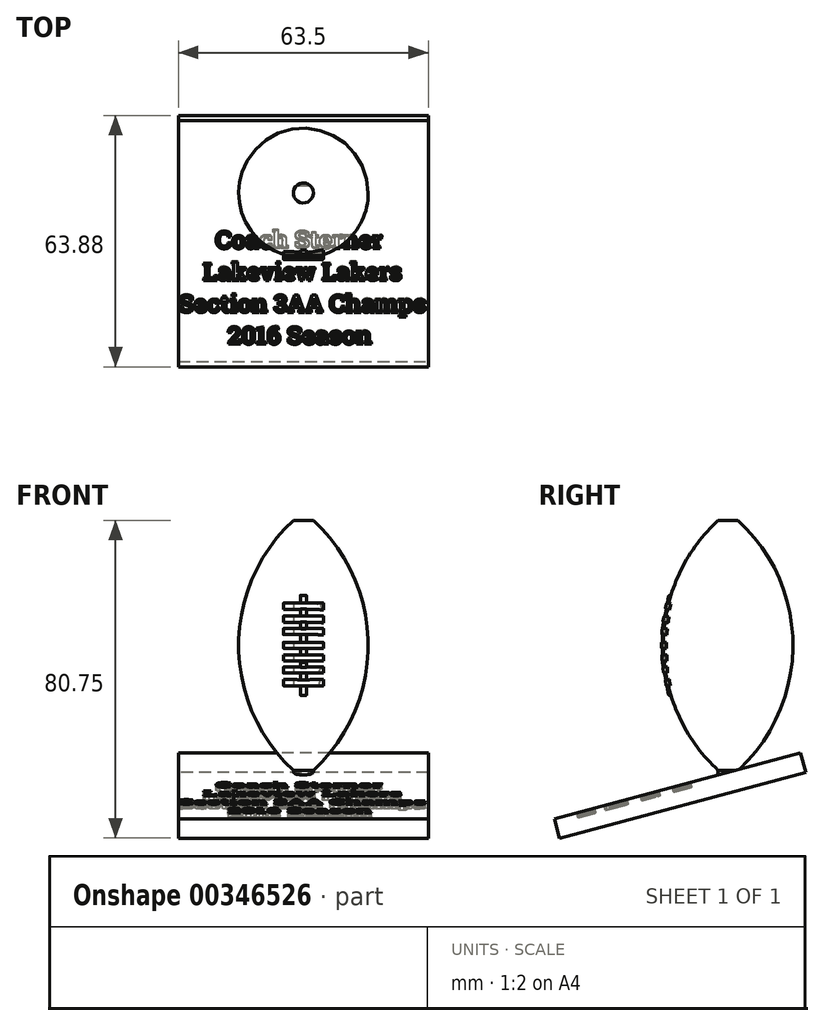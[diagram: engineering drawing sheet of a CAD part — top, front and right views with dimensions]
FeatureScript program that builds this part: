
annotation { "Feature Type Name" : "Feature", "Feature Type Description" : "" }
export const myFeature = defineFeature(function(context is Context, id is Id, definition is map)
    precondition{}
    {
        {
            var Q0;
            Q0=qCreatedBy(makeId("Front.planeOp"),FACE);
            var sketch = newSketch(context, id + "F0", { "sketchPlane" : qUnion([Q0])});
            skLineSegment(sketch, "E0", {"start": v(0, 0) * mm, "end": v(0, 63.5) * mm});
            skLineSegment(sketch, "E1", {"start": v(0, 0) * mm, "end": v(2.54, 0) * mm});
            skLineSegment(sketch, "E2", {"start": v(2.54, 0) * mm, "end": v(2.54, 63.5) * mm});
            skLineSegment(sketch, "E3", {"start": v(2.54, 63.5) * mm, "end": v(0, 63.5) * mm});
            skArc(sketch, "E4", {"start": v(0, 63.5) * mm, "mid": v(-13.91, 31.75) * mm, "end": v(0, 0) * mm});
            skSolve(sketch);
        }
        {
            var Q0;
            Q0=makeQuery(id+"F0.imprint","IMPRINT",FACE,{"disambiguationData":[TD([[makeQuery(id+"F0.imprint","IMPRINT",EDGE,{"derivedFrom":sQuery(id+"F0.wireOp",EDGE,"E0")}),1.0]])]});
            var Q1;
            Q1=sQuery(id+"F0.wireOp",EDGE,"E2");
            revolve(context, id + "F1", {"entities" : qUnion([Q0]), "axis" : qUnion([Q1]), "revolveType" : RevolveType.FULL});
        }
        {
            var Q0;
            Q0=qCreatedBy(makeId("Front.planeOp"),FACE);
            var sketch = newSketch(context, id + "F2", { "sketchPlane" : qUnion([Q0])});
            skLineSegment(sketch, "E5", {"start": v(0, 63.5) * mm, "end": v(2.54, 63.5) * mm});
            skLineSegment(sketch, "E6", {"start": v(0, 63.5) * mm, "end": v(2.03, 65.95) * mm});
            skLineSegment(sketch, "E7", {"start": v(2.03, 65.95) * mm, "end": v(2.54, 65.95) * mm});
            skLineSegment(sketch, "E8", {"start": v(2.54, 65.95) * mm, "end": v(2.54, 63.5) * mm});
            skLineSegment(sketch, "E9.left", {"start": v(0, 63.5) * mm, "end": v(0, 0) * mm});
            skLineSegment(sketch, "E9.right", {"start": v(2.54, 63.5) * mm, "end": v(2.54, 0) * mm});
            skLineSegment(sketch, "E10.bottom", {"start": v(0, 0) * mm, "end": v(2.54, 0) * mm});
            skLineSegment(sketch, "E10.top", {"start": v(0, -2.54) * mm, "end": v(2.54, -2.54) * mm});
            skLineSegment(sketch, "E10.left", {"start": v(0, 0) * mm, "end": v(0, -2.54) * mm});
            skLineSegment(sketch, "E10.right", {"start": v(2.54, 0) * mm, "end": v(2.54, -2.54) * mm});
            skSolve(sketch);
        }
        {
            var Q0;
            Q0=makeQuery(id+"F2.imprint","IMPRINT",FACE,{"disambiguationData":[TD([[makeQuery(id+"F2.imprint","IMPRINT",EDGE,{"derivedFrom":sQuery(id+"F2.wireOp",EDGE,"E5")}),-1.0]])]});
            var Q1;
            Q1=sQuery(id+"F2.wireOp",EDGE,"E9.right");
            revolve(context, id + "F3", {"operationType" : NewBodyOperationType.ADD, "entities" : qUnion([Q0]), "axis" : qUnion([Q1]), "revolveType" : RevolveType.FULL});
        }
        {
            var Q0;
            Q0=makeQuery(id+"F3.opRevolve","SWEPT_FACE",FACE,{"disambiguationData":[OSD([sQuery(id+"F2.wireOp",EDGE,"E10.bottom")])]});
            var sketch = newSketch(context, id + "F4", { "sketchPlane" : qUnion([Q0])});
            skLineSegment(sketch, "E11.bottom", {"start": v(4.34, -1.8) * mm, "end": v(0.74, -1.8) * mm});
            skLineSegment(sketch, "E11.top", {"start": v(4.34, 1.8) * mm, "end": v(0.74, 1.8) * mm});
            skLineSegment(sketch, "E11.left", {"start": v(4.34, -1.8) * mm, "end": v(4.34, 1.8) * mm});
            skLineSegment(sketch, "E11.right", {"start": v(0.74, -1.8) * mm, "end": v(0.74, 1.8) * mm});
            skPoint(sketch, "E11.middle", {"position": v(2.54, 0) * mm});
            skSolve(sketch);
        }
        {
            var Q0;
            Q0=makeQuery(id+"F4.imprint","IMPRINT",FACE,{"disambiguationData":[TD([[makeQuery(id+"F4.imprint","IMPRINT",EDGE,{"derivedFrom":sQuery(id+"F4.wireOp",EDGE,"E11.bottom")}),-1.0]])]});
            extrude(context, id + "F5", {"entities" : qUnion([Q0]), "operationType" : NewBodyOperationType.ADD, "depth" : 2.54 * mm});
        }
        {
            var Q0;
            Q0=makeQuery(id+"F5.opExtrude","CAP_EDGE",EDGE,{"disambiguationData":[OSD([sQuery(id+"F4.wireOp",EDGE,"E11.bottom")])],"isStart":false});
            chamfer(context, id + "F6", {"entities" : qUnion([Q0]), "chamferType" : ChamferType.OFFSET_ANGLE, "width" : 9.4 * mm, "oppositeDirection" : true, "angle" : 15 * degree, "tangentPropagation" : true});
        }
        {
            var Q0;
            Q0=makeQuery(id+"F6.opChamfer","BLEND_FACE",FACE,{"disambiguationData":[OSD([sQuery(id+"F4.wireOp",EDGE,"E11.bottom")])]});
            var sketch = newSketch(context, id + "F7", { "sketchPlane" : qUnion([Q0])});
            skLineSegment(sketch, "E12", {"start": v(2.54, 0.13) * mm, "end": v(2.54, -18.92) * mm});
            skPoint(sketch, "E12.startSnap0", {"position": v(2.54, 1.99) * mm});
            skPoint(sketch, "E12.startSnap1", {"position": v(0.74, 0.13) * mm});
            skLineSegment(sketch, "E13", {"start": v(2.54, -18.92) * mm, "end": v(-29.21, -18.92) * mm});
            skLineSegment(sketch, "E14", {"start": v(-29.21, -18.92) * mm, "end": v(-29.21, 57.28) * mm});
            skLineSegment(sketch, "E15", {"start": v(2.54, -18.92) * mm, "end": v(34.3, -18.92) * mm});
            skLineSegment(sketch, "E16", {"start": v(34.3, -18.92) * mm, "end": v(34.3, 57.28) * mm});
            skLineSegment(sketch, "E17", {"start": v(34.3, 57.28) * mm, "end": v(-29.21, 57.28) * mm});
            skSolve(sketch);
        }
        {
            var Q0;
            Q0=makeQuery(id+"F7.imprint","IMPRINT",FACE,{"disambiguationData":[TD([[makeQuery(id+"F7.imprint","IMPRINT",EDGE,{"derivedFrom":sQuery(id+"F7.wireOp",EDGE,"E13")}),-1.0]])]});
            var Q1;
            {var subQ0=sQuery(id+"F4.wireOp",EDGE,"E11.bottom");var subQ1=makeQuery(id+"F5.opExtrude","CAP_EDGE",EDGE,{"disambiguationData":[OSD([subQ0])],"isStart":false});Q1=makeQuery(id+"F7.imprint","IMPRINT",FACE,{"disambiguationData":[TD([[makeQuery(id+"F7.imprint","IMPRINT",EDGE,{"derivedFrom":makeQuery(id+"F6.opChamfer","BLEND_EDGE",EDGE,{"blendedFrom":[subQ1,makeQuery(id+"F5.opExtrude","SWEPT_FACE",FACE,{"disambiguationData":[OSD([sQuery(id+"F4.wireOp",EDGE,"E11.top")])]})],"blendedInto":[makeQuery(id+"F5.opExtrude","SWEPT_FACE",FACE,{"disambiguationData":[OSD([sQuery(id+"F4.wireOp",EDGE,"E11.top")])]})]})}),-1.0]])]});}
            extrude(context, id + "F8", {"entities" : qUnion([Q0, Q1]), "operationType" : NewBodyOperationType.ADD, "depth" : 5.08 * mm});
        }
        {
            var Q0;
            {var subQ0=makeQuery(id+"F3.opRevolve","SWEPT_FACE",FACE,{"disambiguationData":[OSD([sQuery(id+"F2.wireOp",EDGE,"E10.bottom")])]});Q0=makeQuery(id+"F5.boolean.opBoolean","SPLIT",FACE,{"disambiguationData":[TD([makeQuery(id+"F1.opRevolve","SWEPT_FACE",FACE,{"disambiguationData":[OSD([sQuery(id+"F0.wireOp",EDGE,"E4")])]}),subQ0,makeQuery(id+"F5.opExtrude","SWEPT_FACE",FACE,{"disambiguationData":[OSD([sQuery(id+"F4.wireOp",EDGE,"E11.bottom")])]}),makeQuery(id+"F5.opExtrude","SWEPT_FACE",FACE,{"disambiguationData":[OSD([sQuery(id+"F4.wireOp",EDGE,"E11.top")])]}),makeQuery(id+"F5.opExtrude","SWEPT_FACE",FACE,{"disambiguationData":[OSD([sQuery(id+"F4.wireOp",EDGE,"E11.right")])]})])],"derivedFrom":subQ0});}
            var Q1;
            {var subQ0=makeQuery(id+"F3.opRevolve","SWEPT_FACE",FACE,{"disambiguationData":[OSD([sQuery(id+"F2.wireOp",EDGE,"E10.bottom")])]});Q1=makeQuery(id+"F5.boolean.opBoolean","SPLIT",FACE,{"disambiguationData":[TD([makeQuery(id+"F1.opRevolve","SWEPT_FACE",FACE,{"disambiguationData":[OSD([sQuery(id+"F0.wireOp",EDGE,"E4")])]}),subQ0,makeQuery(id+"F5.opExtrude","SWEPT_FACE",FACE,{"disambiguationData":[OSD([sQuery(id+"F4.wireOp",EDGE,"E11.top")])]}),makeQuery(id+"F5.opExtrude","SWEPT_FACE",FACE,{"disambiguationData":[OSD([sQuery(id+"F4.wireOp",EDGE,"E11.left")])]}),makeQuery(id+"F5.opExtrude","SWEPT_FACE",FACE,{"disambiguationData":[OSD([sQuery(id+"F4.wireOp",EDGE,"E11.right")])]})])],"derivedFrom":subQ0});}
            var Q2;
            {var subQ0=makeQuery(id+"F3.opRevolve","SWEPT_FACE",FACE,{"disambiguationData":[OSD([sQuery(id+"F2.wireOp",EDGE,"E10.bottom")])]});Q2=makeQuery(id+"F5.boolean.opBoolean","SPLIT",FACE,{"disambiguationData":[TD([makeQuery(id+"F1.opRevolve","SWEPT_FACE",FACE,{"disambiguationData":[OSD([sQuery(id+"F0.wireOp",EDGE,"E4")])]}),subQ0,makeQuery(id+"F5.opExtrude","SWEPT_FACE",FACE,{"disambiguationData":[OSD([sQuery(id+"F4.wireOp",EDGE,"E11.bottom")])]}),makeQuery(id+"F5.opExtrude","SWEPT_FACE",FACE,{"disambiguationData":[OSD([sQuery(id+"F4.wireOp",EDGE,"E11.top")])]}),makeQuery(id+"F5.opExtrude","SWEPT_FACE",FACE,{"disambiguationData":[OSD([sQuery(id+"F4.wireOp",EDGE,"E11.left")])]})])],"derivedFrom":subQ0});}
            extrude(context, id + "F9", {"entities" : qUnion([Q0, Q1, Q2]), "operationType" : NewBodyOperationType.ADD, "depth" : 2.54 * mm});
        }
        {
            var Q0;
            Q0=makeQuery(id+"F8.opExtrude","CAP_FACE",FACE,{"disambiguationData":[OSD([sQuery(id+"F7.wireOp",EDGE,"E13"),sQuery(id+"F7.wireOp",EDGE,"E14"),sQuery(id+"F7.wireOp",EDGE,"E15"),sQuery(id+"F7.wireOp",EDGE,"E16"),sQuery(id+"F7.wireOp",EDGE,"E17")])],"isStart":true});
            var sketch = newSketch(context, id + "F10", { "sketchPlane" : qUnion([Q0])});
            skText(sketch, "E18", { "text": "      Coach Sterner\n    Lakeview Lakers\nSection 3AA Champs \n        2016 Season\n", "fontName": "RobotoSlab-Bold.ttf"});
            const initialGuessF10  = {"E18": [-0.02917, -0.01476, 1, 0, 0.00457]};
            skSetInitialGuess(sketch, initialGuessF10);
            skSolve(sketch);
        }
        {
            var Q0;
            Q0 = qSketchRegion(id + "F10", true);
            extrude(context, id + "F11", {"entities" : qUnion([Q0]), "operationType" : NewBodyOperationType.REMOVE, "oppositeDirection" : true, "depth" : 1.27 * mm});
        }
        {
            var Q0;
            {var subQ0=sQuery(id+"F0.wireOp",EDGE,"E4");var subQ1=makeQuery(id+"F1.opRevolve","SWEPT_FACE",FACE,{"disambiguationData":[OSD([subQ0])]});var subQ13=sQuery(id+"F7.wireOp",EDGE,"E17");var subQ14=sQuery(id+"F7.wireOp",EDGE,"E14");var subQ15=sQuery(id+"F7.wireOp",EDGE,"E16");var subQ16=sQuery(id+"F7.wireOp",EDGE,"E15");var subQ17=sQuery(id+"F7.wireOp",EDGE,"E13");Q0=makeQuery(id+"F11.boolean.opBoolean","SPLIT",FACE,{"disambiguationData":[TD([subQ1])],"derivedFrom":makeQuery(id+"F8.opExtrude","CAP_FACE",FACE,{"disambiguationData":[OSD([subQ17,subQ14,subQ16,subQ15,subQ13])],"isStart":true})});}
            var sketch = newSketch(context, id + "F12", { "sketchPlane" : qUnion([Q0])});
            skLineSegment(sketch, "E19.bottom", {"start": v(34.3, -57.28) * mm, "end": v(-29.21, -57.28) * mm});
            skLineSegment(sketch, "E19.top", {"start": v(34.29, -45.85) * mm, "end": v(-29.21, -45.85) * mm});
            skLineSegment(sketch, "E19.left", {"start": v(34.3, -57.28) * mm, "end": v(34.3, -45.85) * mm});
            skLineSegment(sketch, "E19.right", {"start": v(-29.21, -57.28) * mm, "end": v(-29.21, -45.85) * mm});
            skSolve(sketch);
        }
        {
            var Q0;
            Q0=makeQuery(id+"F12.imprint","IMPRINT",FACE,{"disambiguationData":[TD([[makeQuery(id+"F12.imprint","IMPRINT",EDGE,{"derivedFrom":sQuery(id+"F12.wireOp",EDGE,"E19.bottom")}),-1.0]])]});
            extrude(context, id + "F13", {"entities" : qUnion([Q0]), "operationType" : NewBodyOperationType.REMOVE, "oppositeDirection" : true, "depth" : 25.4 * mm});
        }
        {
            var Q0;
            Q0=qCreatedBy(makeId("Right.planeOp"),FACE);
            var sketch = newSketch(context, id + "F14", { "sketchPlane" : qUnion([Q0])});
            skLineSegment(sketch, "E20", {"start": v(0, 0) * mm, "end": v(0, 63.5) * mm});
            skLineSegment(sketch, "E21", {"start": v(0, 63.5) * mm, "end": v(-3.05, 63.5) * mm});
            skLineSegment(sketch, "E22", {"start": v(-3.05, 63.5) * mm, "end": v(-3.05, 0) * mm});
            skLineSegment(sketch, "E23", {"start": v(-3.05, 0) * mm, "end": v(0, 0) * mm});
            skArc(sketch, "E24", {"start": v(-3.05, 63.5) * mm, "mid": v(-16.96, 31.75) * mm, "end": v(-3.05, 0) * mm});
            skLineSegment(sketch, "E25.bottom", {"start": v(-16.96, 32.51) * mm, "end": v(-15.63, 32.51) * mm});
            skLineSegment(sketch, "E25.top", {"start": v(-16.96, 30.99) * mm, "end": v(-15.63, 30.99) * mm});
            skLineSegment(sketch, "E25.left", {"start": v(-16.96, 32.51) * mm, "end": v(-16.96, 30.99) * mm});
            skLineSegment(sketch, "E25.right", {"start": v(-15.63, 32.51) * mm, "end": v(-15.63, 30.99) * mm});
            skLineSegment(sketch, "E26", {"start": v(-15.2, 34.39) * mm, "end": v(-15.08, 35.9) * mm});
            skLineSegment(sketch, "E27", {"start": v(-15.08, 35.9) * mm, "end": v(-16.75, 36.04) * mm});
            skLineSegment(sketch, "E28", {"start": v(-16.75, 36.04) * mm, "end": v(-16.87, 34.52) * mm});
            skLineSegment(sketch, "E29", {"start": v(-16.87, 34.52) * mm, "end": v(-15.2, 34.39) * mm});
            skLineSegment(sketch, "E30", {"start": v(-16.55, 37.68) * mm, "end": v(-16.32, 39.19) * mm});
            skLineSegment(sketch, "E31", {"start": v(-16.32, 39.19) * mm, "end": v(-14.98, 38.98) * mm});
            skLineSegment(sketch, "E32", {"start": v(-14.98, 38.98) * mm, "end": v(-15.21, 37.47) * mm});
            skLineSegment(sketch, "E33", {"start": v(-15.21, 37.47) * mm, "end": v(-16.55, 37.68) * mm});
            skLineSegment(sketch, "E34", {"start": v(-16.9, 29.29) * mm, "end": v(-15.57, 29.29) * mm});
            skLineSegment(sketch, "E35", {"start": v(-15.57, 29.29) * mm, "end": v(-15.57, 27.77) * mm});
            skLineSegment(sketch, "E36", {"start": v(-15.57, 27.77) * mm, "end": v(-16.78, 27.77) * mm});
            skLineSegment(sketch, "E37", {"start": v(-16.78, 27.77) * mm, "end": v(-16.9, 29.29) * mm});
            skLineSegment(sketch, "E38", {"start": v(-16.6, 26.22) * mm, "end": v(-15.46, 26.22) * mm});
            skLineSegment(sketch, "E39", {"start": v(-15.46, 26.22) * mm, "end": v(-15.46, 24.7) * mm});
            skLineSegment(sketch, "E40", {"start": v(-15.46, 24.7) * mm, "end": v(-16.38, 24.7) * mm});
            skLineSegment(sketch, "E41", {"start": v(-16.38, 24.7) * mm, "end": v(-16.6, 26.22) * mm});
            skLineSegment(sketch, "E42", {"start": v(-15.95, 41.04) * mm, "end": v(-15.6, 42.52) * mm});
            skLineSegment(sketch, "E43", {"start": v(-15.6, 42.52) * mm, "end": v(-14.5, 42.26) * mm});
            skLineSegment(sketch, "E44", {"start": v(-14.5, 42.26) * mm, "end": v(-14.86, 40.78) * mm});
            skLineSegment(sketch, "E45", {"start": v(-14.86, 40.78) * mm, "end": v(-15.95, 41.04) * mm});
            skLineSegment(sketch, "E46", {"start": v(-16.05, 22.93) * mm, "end": v(-15.7, 21.42) * mm});
            skLineSegment(sketch, "E47", {"start": v(-15.7, 21.42) * mm, "end": v(-14.71, 21.6) * mm});
            skLineSegment(sketch, "E48", {"start": v(-14.71, 21.6) * mm, "end": v(-14.98, 23.1) * mm});
            skLineSegment(sketch, "E49", {"start": v(-14.98, 23.1) * mm, "end": v(-16.05, 22.93) * mm});
            skSolve(sketch);
        }
        {
            var Q0;
            Q0=makeQuery(id+"F14.imprint","IMPRINT",FACE,{"disambiguationData":[TD([[makeQuery(id+"F14.imprint","IMPRINT",EDGE,{"derivedFrom":sQuery(id+"F14.wireOp",EDGE,"E42")}),-1.0]])]});
            var Q1;
            {var subQ0=sQuery(id+"F14.wireOp",EDGE,"E32");Q1=makeQuery(id+"F14.imprint","IMPRINT",FACE,{"disambiguationData":[TD([[makeQuery(id+"F14.imprint","IMPRINT",EDGE,{"derivedFrom":subQ0}),-1.0]])]});}
            var Q2;
            Q2=makeQuery(id+"F14.imprint","IMPRINT",FACE,{"disambiguationData":[TD([[makeQuery(id+"F14.imprint","IMPRINT",EDGE,{"derivedFrom":sQuery(id+"F14.wireOp",EDGE,"E26")}),1.0]])]});
            var Q3;
            Q3=makeQuery(id+"F14.imprint","IMPRINT",FACE,{"disambiguationData":[TD([[makeQuery(id+"F14.imprint","IMPRINT",EDGE,{"derivedFrom":sQuery(id+"F14.wireOp",EDGE,"E25.bottom")}),-1.0]])]});
            var Q4;
            Q4=makeQuery(id+"F14.imprint","IMPRINT",FACE,{"disambiguationData":[TD([[makeQuery(id+"F14.imprint","IMPRINT",EDGE,{"derivedFrom":sQuery(id+"F14.wireOp",EDGE,"E34")}),-1.0]])]});
            var Q5;
            Q5=makeQuery(id+"F14.imprint","IMPRINT",FACE,{"disambiguationData":[TD([[makeQuery(id+"F14.imprint","IMPRINT",EDGE,{"derivedFrom":sQuery(id+"F14.wireOp",EDGE,"E38")}),-1.0]])]});
            var Q6;
            Q6=makeQuery(id+"F14.imprint","IMPRINT",FACE,{"disambiguationData":[TD([[makeQuery(id+"F14.imprint","IMPRINT",EDGE,{"derivedFrom":sQuery(id+"F14.wireOp",EDGE,"E46")}),1.0]])]});
            extrude(context, id + "F15", {"entities" : qUnion([Q0, Q1, Q2, Q3, Q4, Q5, Q6]), "operationType" : NewBodyOperationType.ADD, "depth" : 7.62 * mm});
        }
        {
            var Q0;
            Q0=makeQuery(id+"F15.opExtrude","CAP_FACE",FACE,{"disambiguationData":[OSD([sQuery(id+"F14.wireOp",EDGE,"E42"),sQuery(id+"F14.wireOp",EDGE,"E43"),sQuery(id+"F14.wireOp",EDGE,"E44"),sQuery(id+"F14.wireOp",EDGE,"E45")])],"isStart":true});
            var Q1;
            Q1=makeQuery(id+"F15.opExtrude","CAP_FACE",FACE,{"disambiguationData":[OSD([sQuery(id+"F14.wireOp",EDGE,"E24"),sQuery(id+"F14.wireOp",EDGE,"E30"),sQuery(id+"F14.wireOp",EDGE,"E31"),sQuery(id+"F14.wireOp",EDGE,"E32"),sQuery(id+"F14.wireOp",EDGE,"E33")])],"isStart":true});
            var Q2;
            Q2=makeQuery(id+"F15.opExtrude","CAP_FACE",FACE,{"disambiguationData":[OSD([sQuery(id+"F14.wireOp",EDGE,"E26"),sQuery(id+"F14.wireOp",EDGE,"E27"),sQuery(id+"F14.wireOp",EDGE,"E28"),sQuery(id+"F14.wireOp",EDGE,"E29")])],"isStart":true});
            var Q3;
            Q3=makeQuery(id+"F15.opExtrude","CAP_FACE",FACE,{"disambiguationData":[OSD([sQuery(id+"F14.wireOp",EDGE,"E25.bottom"),sQuery(id+"F14.wireOp",EDGE,"E25.top"),sQuery(id+"F14.wireOp",EDGE,"E25.left"),sQuery(id+"F14.wireOp",EDGE,"E25.right")])],"isStart":true});
            var Q4;
            Q4=makeQuery(id+"F15.opExtrude","CAP_FACE",FACE,{"disambiguationData":[OSD([sQuery(id+"F14.wireOp",EDGE,"E34"),sQuery(id+"F14.wireOp",EDGE,"E35"),sQuery(id+"F14.wireOp",EDGE,"E36"),sQuery(id+"F14.wireOp",EDGE,"E37")])],"isStart":true});
            var Q5;
            Q5=makeQuery(id+"F15.opExtrude","CAP_FACE",FACE,{"disambiguationData":[OSD([sQuery(id+"F14.wireOp",EDGE,"E38"),sQuery(id+"F14.wireOp",EDGE,"E39"),sQuery(id+"F14.wireOp",EDGE,"E40"),sQuery(id+"F14.wireOp",EDGE,"E41")])],"isStart":true});
            var Q6;
            Q6=makeQuery(id+"F15.opExtrude","CAP_FACE",FACE,{"disambiguationData":[OSD([sQuery(id+"F14.wireOp",EDGE,"E46"),sQuery(id+"F14.wireOp",EDGE,"E47"),sQuery(id+"F14.wireOp",EDGE,"E48"),sQuery(id+"F14.wireOp",EDGE,"E49")])],"isStart":true});
            extrude(context, id + "F16", {"entities" : qUnion([Q0, Q1, Q2, Q3, Q4, Q5, Q6]), "operationType" : NewBodyOperationType.ADD, "depth" : 2.54 * mm});
        }
        {
            var Q0;
            {var subQ0=sQuery(id+"F14.wireOp",EDGE,"E25.left");Q0=makeQuery(id+"F16.boolean.opBoolean","MERGE",FACE,{"derivedFrom":[makeQuery(id+"F15.opExtrude","SWEPT_FACE",FACE,{"disambiguationData":[OSD([subQ0])]}),makeQuery(id+"F16.opExtrude","SWEPT_FACE",FACE,{"disambiguationData":[OSD([subQ0])]})]});}
            var sketch = newSketch(context, id + "F17", { "sketchPlane" : qUnion([Q0])});
            skLineSegment(sketch, "E50.bottom", {"start": v(3.3, 19.05) * mm, "end": v(1.78, 19.05) * mm});
            skLineSegment(sketch, "E50.top", {"start": v(3.3, 44.45) * mm, "end": v(1.78, 44.45) * mm});
            skLineSegment(sketch, "E50.left", {"start": v(3.3, 19.05) * mm, "end": v(3.3, 44.45) * mm});
            skLineSegment(sketch, "E50.right", {"start": v(1.78, 19.05) * mm, "end": v(1.78, 44.45) * mm});
            skPoint(sketch, "E50.middle", {"position": v(2.54, 31.75) * mm});
            skPoint(sketch, "E50.middle.positionSnap0", {"position": v(7.62, 31.75) * mm});
            skPoint(sketch, "E50.middle.positionSnap1", {"position": v(2.54, 32.51) * mm});
            skPoint(sketch, "E50.centerSnap0", {"position": v(7.62, 31.75) * mm});
            skPoint(sketch, "E50.centerSnap1", {"position": v(2.54, 32.51) * mm});
            skSolve(sketch);
        }
        {
            var Q0;
            {var subQ0=sQuery(id+"F17.wireOp",EDGE,"E50.top");Q0=makeQuery(id+"F17.imprint","IMPRINT",FACE,{"disambiguationData":[TD([[makeQuery(id+"F17.imprint","IMPRINT",EDGE,{"derivedFrom":subQ0}),1.0]])]});}
            var Q1;
            {var subQ0=sQuery(id+"F17.wireOp",EDGE,"E50.bottom");Q1=makeQuery(id+"F17.imprint","IMPRINT",FACE,{"disambiguationData":[TD([[makeQuery(id+"F17.imprint","IMPRINT",EDGE,{"derivedFrom":subQ0}),-1.0]])]});}
            var Q2;
            {var subQ0=sQuery(id+"F17.wireOp",EDGE,"E50.left");var subQ1=sQuery(id+"F14.wireOp",EDGE,"E25.left");var subQ2=sQuery(id+"F14.wireOp",EDGE,"E25.top");var subQ3=sQuery(id+"F14.wireOp",EDGE,"E24");var subQ4=makeQuery(id+"F16.boolean.opBoolean","MERGE",EDGE,{"derivedFrom":[makeQuery(id+"F15.opExtrude","SWEPT_EDGE",EDGE,{"disambiguationData":[OSD([subQ3,subQ2,subQ1])]}),makeQuery(id+"F16.opExtrude","SWEPT_EDGE",EDGE,{"disambiguationData":[OSD([subQ3,subQ2,subQ1])]})]});var subQ5=makeQuery(id+"F17.imprint","INTERSECT",VERTEX,{"derivedFrom":[subQ4,subQ0]});Q2=makeQuery(id+"F17.imprint","IMPRINT",FACE,{"disambiguationData":[TD([[makeQuery(id+"F17.imprint","IMPRINT",EDGE,{"disambiguationData":[TD([[subQ5,-1.0]])],"derivedFrom":subQ0}),1.0]])]});}
            extrude(context, id + "F18", {"entities" : qUnion([Q0, Q1, Q2]), "operationType" : NewBodyOperationType.ADD, "oppositeDirection" : true, "depth" : 2.54 * mm});
        }
        {
            var Q0;
            {var subQ0=sQuery(id+"F14.wireOp",EDGE,"E31");var subQ1=sQuery(id+"F14.wireOp",EDGE,"E24");Q0=makeQuery(id+"F18.boolean.opBoolean","SPLIT",EDGE,{"disambiguationData":[TD([makeQuery(id+"F18.opExtrude","SWEPT_FACE",FACE,{"disambiguationData":[OSD([sQuery(id+"F17.wireOp",EDGE,"E50.left")])]})])],"derivedFrom":makeQuery(id+"F16.boolean.opBoolean","MERGE",EDGE,{"derivedFrom":[makeQuery(id+"F15.opExtrude","SWEPT_EDGE",EDGE,{"disambiguationData":[OSD([subQ1,subQ0])]}),makeQuery(id+"F16.opExtrude","SWEPT_EDGE",EDGE,{"disambiguationData":[OSD([subQ1,subQ0])]})]})});}
            var Q1;
            Q1=makeQuery(id+"F15.opExtrude","CAP_EDGE",EDGE,{"disambiguationData":[OSD([sQuery(id+"F14.wireOp",EDGE,"E30")])],"isStart":false});
            var Q2;
            {var subQ0=sQuery(id+"F14.wireOp",EDGE,"E33");var subQ1=sQuery(id+"F14.wireOp",EDGE,"E30");var subQ2=sQuery(id+"F14.wireOp",EDGE,"E24");Q2=makeQuery(id+"F18.boolean.opBoolean","SPLIT",EDGE,{"disambiguationData":[TD([makeQuery(id+"F18.opExtrude","SWEPT_FACE",FACE,{"disambiguationData":[OSD([sQuery(id+"F17.wireOp",EDGE,"E50.left")])]})])],"derivedFrom":makeQuery(id+"F16.boolean.opBoolean","MERGE",EDGE,{"derivedFrom":[makeQuery(id+"F15.opExtrude","SWEPT_EDGE",EDGE,{"disambiguationData":[OSD([subQ2,subQ1,subQ0])]}),makeQuery(id+"F16.opExtrude","SWEPT_EDGE",EDGE,{"disambiguationData":[OSD([subQ2,subQ1,subQ0])]})]})});}
            var Q3;
            {var subQ0=sQuery(id+"F14.wireOp",EDGE,"E31");var subQ1=sQuery(id+"F14.wireOp",EDGE,"E24");Q3=makeQuery(id+"F18.boolean.opBoolean","SPLIT",EDGE,{"disambiguationData":[TD([makeQuery(id+"F18.opExtrude","SWEPT_FACE",FACE,{"disambiguationData":[OSD([sQuery(id+"F17.wireOp",EDGE,"E50.right")])]})])],"derivedFrom":makeQuery(id+"F16.boolean.opBoolean","MERGE",EDGE,{"derivedFrom":[makeQuery(id+"F15.opExtrude","SWEPT_EDGE",EDGE,{"disambiguationData":[OSD([subQ1,subQ0])]}),makeQuery(id+"F16.opExtrude","SWEPT_EDGE",EDGE,{"disambiguationData":[OSD([subQ1,subQ0])]})]})});}
            var Q4;
            {var subQ0=sQuery(id+"F14.wireOp",EDGE,"E33");var subQ1=sQuery(id+"F14.wireOp",EDGE,"E30");var subQ2=sQuery(id+"F14.wireOp",EDGE,"E24");Q4=makeQuery(id+"F18.boolean.opBoolean","SPLIT",EDGE,{"disambiguationData":[TD([makeQuery(id+"F18.opExtrude","SWEPT_FACE",FACE,{"disambiguationData":[OSD([sQuery(id+"F17.wireOp",EDGE,"E50.right")])]})])],"derivedFrom":makeQuery(id+"F16.boolean.opBoolean","MERGE",EDGE,{"derivedFrom":[makeQuery(id+"F15.opExtrude","SWEPT_EDGE",EDGE,{"disambiguationData":[OSD([subQ2,subQ1,subQ0])]}),makeQuery(id+"F16.opExtrude","SWEPT_EDGE",EDGE,{"disambiguationData":[OSD([subQ2,subQ1,subQ0])]})]})});}
            var Q5;
            Q5=makeQuery(id+"F16.opExtrude","CAP_EDGE",EDGE,{"disambiguationData":[OSD([sQuery(id+"F14.wireOp",EDGE,"E30")])],"isStart":false});
            var Q6;
            Q6=makeQuery(id+"F16.opExtrude","CAP_EDGE",EDGE,{"disambiguationData":[OSD([sQuery(id+"F14.wireOp",EDGE,"E24")])],"isStart":false});
            var Q7;
            Q7=makeQuery(id+"F15.opExtrude","CAP_EDGE",EDGE,{"disambiguationData":[OSD([sQuery(id+"F14.wireOp",EDGE,"E24")])],"isStart":false});
            var Q8;
            {var subQ0=sQuery(id+"F14.wireOp",EDGE,"E43");var subQ1=sQuery(id+"F14.wireOp",EDGE,"E42");var subQ2=sQuery(id+"F14.wireOp",EDGE,"E24");Q8=makeQuery(id+"F18.boolean.opBoolean","SPLIT",EDGE,{"disambiguationData":[TD([makeQuery(id+"F18.opExtrude","SWEPT_FACE",FACE,{"disambiguationData":[OSD([sQuery(id+"F17.wireOp",EDGE,"E50.right")])]})])],"derivedFrom":makeQuery(id+"F16.boolean.opBoolean","MERGE",EDGE,{"derivedFrom":[makeQuery(id+"F15.opExtrude","SWEPT_EDGE",EDGE,{"disambiguationData":[OSD([subQ2,subQ1,subQ0])]}),makeQuery(id+"F16.opExtrude","SWEPT_EDGE",EDGE,{"disambiguationData":[OSD([subQ2,subQ1,subQ0])]})]})});}
            var Q9;
            {var subQ0=sQuery(id+"F14.wireOp",EDGE,"E42");var subQ1=sQuery(id+"F14.wireOp",EDGE,"E45");var subQ2=sQuery(id+"F14.wireOp",EDGE,"E24");Q9=makeQuery(id+"F18.boolean.opBoolean","SPLIT",EDGE,{"disambiguationData":[TD([makeQuery(id+"F18.opExtrude","SWEPT_FACE",FACE,{"disambiguationData":[OSD([sQuery(id+"F17.wireOp",EDGE,"E50.right")])]})])],"derivedFrom":makeQuery(id+"F16.boolean.opBoolean","MERGE",EDGE,{"derivedFrom":[makeQuery(id+"F15.opExtrude","SWEPT_EDGE",EDGE,{"disambiguationData":[OSD([subQ2,subQ0,subQ1])]}),makeQuery(id+"F16.opExtrude","SWEPT_EDGE",EDGE,{"disambiguationData":[OSD([subQ2,subQ0,subQ1])]})]})});}
            var Q10;
            Q10=makeQuery(id+"F16.opExtrude","CAP_EDGE",EDGE,{"disambiguationData":[OSD([sQuery(id+"F14.wireOp",EDGE,"E42")])],"isStart":false});
            var Q11;
            {var subQ0=sQuery(id+"F14.wireOp",EDGE,"E43");var subQ1=sQuery(id+"F14.wireOp",EDGE,"E42");var subQ2=sQuery(id+"F14.wireOp",EDGE,"E24");Q11=makeQuery(id+"F18.boolean.opBoolean","SPLIT",EDGE,{"disambiguationData":[TD([makeQuery(id+"F18.opExtrude","SWEPT_FACE",FACE,{"disambiguationData":[OSD([sQuery(id+"F17.wireOp",EDGE,"E50.left")])]})])],"derivedFrom":makeQuery(id+"F16.boolean.opBoolean","MERGE",EDGE,{"derivedFrom":[makeQuery(id+"F15.opExtrude","SWEPT_EDGE",EDGE,{"disambiguationData":[OSD([subQ2,subQ1,subQ0])]}),makeQuery(id+"F16.opExtrude","SWEPT_EDGE",EDGE,{"disambiguationData":[OSD([subQ2,subQ1,subQ0])]})]})});}
            var Q12;
            {var subQ0=sQuery(id+"F14.wireOp",EDGE,"E42");var subQ1=sQuery(id+"F14.wireOp",EDGE,"E45");var subQ2=sQuery(id+"F14.wireOp",EDGE,"E24");Q12=makeQuery(id+"F18.boolean.opBoolean","SPLIT",EDGE,{"disambiguationData":[TD([makeQuery(id+"F18.opExtrude","SWEPT_FACE",FACE,{"disambiguationData":[OSD([sQuery(id+"F17.wireOp",EDGE,"E50.left")])]})])],"derivedFrom":makeQuery(id+"F16.boolean.opBoolean","MERGE",EDGE,{"derivedFrom":[makeQuery(id+"F15.opExtrude","SWEPT_EDGE",EDGE,{"disambiguationData":[OSD([subQ2,subQ0,subQ1])]}),makeQuery(id+"F16.opExtrude","SWEPT_EDGE",EDGE,{"disambiguationData":[OSD([subQ2,subQ0,subQ1])]})]})});}
            var Q13;
            Q13=makeQuery(id+"F15.opExtrude","CAP_EDGE",EDGE,{"disambiguationData":[OSD([sQuery(id+"F14.wireOp",EDGE,"E42")])],"isStart":false});
            var Q14;
            {var subQ0=sQuery(id+"F14.wireOp",EDGE,"E28");var subQ1=sQuery(id+"F14.wireOp",EDGE,"E27");var subQ2=sQuery(id+"F14.wireOp",EDGE,"E24");Q14=makeQuery(id+"F18.boolean.opBoolean","SPLIT",EDGE,{"disambiguationData":[TD([makeQuery(id+"F18.opExtrude","SWEPT_FACE",FACE,{"disambiguationData":[OSD([sQuery(id+"F17.wireOp",EDGE,"E50.right")])]})])],"derivedFrom":makeQuery(id+"F16.boolean.opBoolean","MERGE",EDGE,{"derivedFrom":[makeQuery(id+"F15.opExtrude","SWEPT_EDGE",EDGE,{"disambiguationData":[OSD([subQ2,subQ1,subQ0])]}),makeQuery(id+"F16.opExtrude","SWEPT_EDGE",EDGE,{"disambiguationData":[OSD([subQ2,subQ1,subQ0])]})]})});}
            var Q15;
            Q15=makeQuery(id+"F16.opExtrude","CAP_EDGE",EDGE,{"disambiguationData":[OSD([sQuery(id+"F14.wireOp",EDGE,"E28")])],"isStart":false});
            var Q16;
            {var subQ0=sQuery(id+"F14.wireOp",EDGE,"E28");var subQ1=sQuery(id+"F14.wireOp",EDGE,"E29");var subQ2=sQuery(id+"F14.wireOp",EDGE,"E24");Q16=makeQuery(id+"F18.boolean.opBoolean","SPLIT",EDGE,{"disambiguationData":[TD([makeQuery(id+"F18.opExtrude","SWEPT_FACE",FACE,{"disambiguationData":[OSD([sQuery(id+"F17.wireOp",EDGE,"E50.right")])]})])],"derivedFrom":makeQuery(id+"F16.boolean.opBoolean","MERGE",EDGE,{"derivedFrom":[makeQuery(id+"F15.opExtrude","SWEPT_EDGE",EDGE,{"disambiguationData":[OSD([subQ2,subQ0,subQ1])]}),makeQuery(id+"F16.opExtrude","SWEPT_EDGE",EDGE,{"disambiguationData":[OSD([subQ2,subQ0,subQ1])]})]})});}
            var Q17;
            {var subQ0=sQuery(id+"F14.wireOp",EDGE,"E28");var subQ1=sQuery(id+"F14.wireOp",EDGE,"E27");var subQ2=sQuery(id+"F14.wireOp",EDGE,"E24");Q17=makeQuery(id+"F18.boolean.opBoolean","SPLIT",EDGE,{"disambiguationData":[TD([makeQuery(id+"F18.opExtrude","SWEPT_FACE",FACE,{"disambiguationData":[OSD([sQuery(id+"F17.wireOp",EDGE,"E50.left")])]})])],"derivedFrom":makeQuery(id+"F16.boolean.opBoolean","MERGE",EDGE,{"derivedFrom":[makeQuery(id+"F15.opExtrude","SWEPT_EDGE",EDGE,{"disambiguationData":[OSD([subQ2,subQ1,subQ0])]}),makeQuery(id+"F16.opExtrude","SWEPT_EDGE",EDGE,{"disambiguationData":[OSD([subQ2,subQ1,subQ0])]})]})});}
            var Q18;
            {var subQ0=sQuery(id+"F14.wireOp",EDGE,"E28");var subQ1=sQuery(id+"F14.wireOp",EDGE,"E29");var subQ2=sQuery(id+"F14.wireOp",EDGE,"E24");Q18=makeQuery(id+"F18.boolean.opBoolean","SPLIT",EDGE,{"disambiguationData":[TD([makeQuery(id+"F18.opExtrude","SWEPT_FACE",FACE,{"disambiguationData":[OSD([sQuery(id+"F17.wireOp",EDGE,"E50.left")])]})])],"derivedFrom":makeQuery(id+"F16.boolean.opBoolean","MERGE",EDGE,{"derivedFrom":[makeQuery(id+"F15.opExtrude","SWEPT_EDGE",EDGE,{"disambiguationData":[OSD([subQ2,subQ0,subQ1])]}),makeQuery(id+"F16.opExtrude","SWEPT_EDGE",EDGE,{"disambiguationData":[OSD([subQ2,subQ0,subQ1])]})]})});}
            var Q19;
            Q19=makeQuery(id+"F15.opExtrude","CAP_EDGE",EDGE,{"disambiguationData":[OSD([sQuery(id+"F14.wireOp",EDGE,"E28")])],"isStart":false});
            var Q20;
            {var subQ0=sQuery(id+"F14.wireOp",EDGE,"E25.bottom");var subQ1=sQuery(id+"F14.wireOp",EDGE,"E25.left");var subQ2=sQuery(id+"F17.wireOp",EDGE,"E50.right");var subQ3=sQuery(id+"F14.wireOp",EDGE,"E24");Q20=makeQuery(id+"F18.boolean.opBoolean","SPLIT",EDGE,{"disambiguationData":[TD([makeQuery(id+"F18.opExtrude","SWEPT_FACE",FACE,{"disambiguationData":[OSD([subQ2])]})])],"derivedFrom":makeQuery(id+"F16.boolean.opBoolean","MERGE",EDGE,{"derivedFrom":[makeQuery(id+"F15.opExtrude","SWEPT_EDGE",EDGE,{"disambiguationData":[OSD([subQ3,subQ0,subQ1])]}),makeQuery(id+"F16.opExtrude","SWEPT_EDGE",EDGE,{"disambiguationData":[OSD([subQ3,subQ0,subQ1])]})]})});}
            var Q21;
            Q21=makeQuery(id+"F16.opExtrude","CAP_EDGE",EDGE,{"disambiguationData":[OSD([sQuery(id+"F14.wireOp",EDGE,"E25.left")])],"isStart":false});
            var Q22;
            {var subQ0=sQuery(id+"F14.wireOp",EDGE,"E25.left");var subQ1=sQuery(id+"F14.wireOp",EDGE,"E25.top");var subQ2=sQuery(id+"F17.wireOp",EDGE,"E50.right");var subQ3=sQuery(id+"F14.wireOp",EDGE,"E24");Q22=makeQuery(id+"F18.boolean.opBoolean","SPLIT",EDGE,{"disambiguationData":[TD([makeQuery(id+"F18.opExtrude","SWEPT_FACE",FACE,{"disambiguationData":[OSD([subQ2])]})])],"derivedFrom":makeQuery(id+"F16.boolean.opBoolean","MERGE",EDGE,{"derivedFrom":[makeQuery(id+"F15.opExtrude","SWEPT_EDGE",EDGE,{"disambiguationData":[OSD([subQ3,subQ1,subQ0])]}),makeQuery(id+"F16.opExtrude","SWEPT_EDGE",EDGE,{"disambiguationData":[OSD([subQ3,subQ1,subQ0])]})]})});}
            var Q23;
            {var subQ0=sQuery(id+"F14.wireOp",EDGE,"E25.left");var subQ1=sQuery(id+"F14.wireOp",EDGE,"E25.top");var subQ2=sQuery(id+"F17.wireOp",EDGE,"E50.left");var subQ3=sQuery(id+"F14.wireOp",EDGE,"E24");Q23=makeQuery(id+"F18.boolean.opBoolean","SPLIT",EDGE,{"disambiguationData":[TD([makeQuery(id+"F18.opExtrude","SWEPT_FACE",FACE,{"disambiguationData":[OSD([subQ2])]})])],"derivedFrom":makeQuery(id+"F16.boolean.opBoolean","MERGE",EDGE,{"derivedFrom":[makeQuery(id+"F15.opExtrude","SWEPT_EDGE",EDGE,{"disambiguationData":[OSD([subQ3,subQ1,subQ0])]}),makeQuery(id+"F16.opExtrude","SWEPT_EDGE",EDGE,{"disambiguationData":[OSD([subQ3,subQ1,subQ0])]})]})});}
            var Q24;
            {var subQ0=sQuery(id+"F14.wireOp",EDGE,"E25.left");var subQ1=sQuery(id+"F14.wireOp",EDGE,"E25.bottom");var subQ2=sQuery(id+"F17.wireOp",EDGE,"E50.left");var subQ3=sQuery(id+"F14.wireOp",EDGE,"E24");Q24=makeQuery(id+"F18.boolean.opBoolean","SPLIT",EDGE,{"disambiguationData":[TD([makeQuery(id+"F18.opExtrude","SWEPT_FACE",FACE,{"disambiguationData":[OSD([subQ2])]})])],"derivedFrom":makeQuery(id+"F16.boolean.opBoolean","MERGE",EDGE,{"derivedFrom":[makeQuery(id+"F15.opExtrude","SWEPT_EDGE",EDGE,{"disambiguationData":[OSD([subQ3,subQ1,subQ0])]}),makeQuery(id+"F16.opExtrude","SWEPT_EDGE",EDGE,{"disambiguationData":[OSD([subQ3,subQ1,subQ0])]})]})});}
            var Q25;
            Q25=makeQuery(id+"F15.opExtrude","CAP_EDGE",EDGE,{"disambiguationData":[OSD([sQuery(id+"F14.wireOp",EDGE,"E25.left")])],"isStart":false});
            var Q26;
            {var subQ0=sQuery(id+"F14.wireOp",EDGE,"E37");var subQ1=sQuery(id+"F14.wireOp",EDGE,"E34");var subQ2=sQuery(id+"F14.wireOp",EDGE,"E24");Q26=makeQuery(id+"F18.boolean.opBoolean","SPLIT",EDGE,{"disambiguationData":[TD([makeQuery(id+"F18.opExtrude","SWEPT_FACE",FACE,{"disambiguationData":[OSD([sQuery(id+"F17.wireOp",EDGE,"E50.left")])]})])],"derivedFrom":makeQuery(id+"F16.boolean.opBoolean","MERGE",EDGE,{"derivedFrom":[makeQuery(id+"F15.opExtrude","SWEPT_EDGE",EDGE,{"disambiguationData":[OSD([subQ2,subQ1,subQ0])]}),makeQuery(id+"F16.opExtrude","SWEPT_EDGE",EDGE,{"disambiguationData":[OSD([subQ2,subQ1,subQ0])]})]})});}
            var Q27;
            {var subQ0=sQuery(id+"F14.wireOp",EDGE,"E37");var subQ1=sQuery(id+"F14.wireOp",EDGE,"E36");var subQ2=sQuery(id+"F14.wireOp",EDGE,"E24");Q27=makeQuery(id+"F18.boolean.opBoolean","SPLIT",EDGE,{"disambiguationData":[TD([makeQuery(id+"F18.opExtrude","SWEPT_FACE",FACE,{"disambiguationData":[OSD([sQuery(id+"F17.wireOp",EDGE,"E50.left")])]})])],"derivedFrom":makeQuery(id+"F16.boolean.opBoolean","MERGE",EDGE,{"derivedFrom":[makeQuery(id+"F15.opExtrude","SWEPT_EDGE",EDGE,{"disambiguationData":[OSD([subQ2,subQ1,subQ0])]}),makeQuery(id+"F16.opExtrude","SWEPT_EDGE",EDGE,{"disambiguationData":[OSD([subQ2,subQ1,subQ0])]})]})});}
            var Q28;
            Q28=makeQuery(id+"F15.opExtrude","CAP_EDGE",EDGE,{"disambiguationData":[OSD([sQuery(id+"F14.wireOp",EDGE,"E37")])],"isStart":false});
            var Q29;
            {var subQ0=sQuery(id+"F14.wireOp",EDGE,"E34");var subQ1=sQuery(id+"F14.wireOp",EDGE,"E37");var subQ2=sQuery(id+"F14.wireOp",EDGE,"E24");Q29=makeQuery(id+"F18.boolean.opBoolean","SPLIT",EDGE,{"disambiguationData":[TD([makeQuery(id+"F18.opExtrude","SWEPT_FACE",FACE,{"disambiguationData":[OSD([sQuery(id+"F17.wireOp",EDGE,"E50.right")])]})])],"derivedFrom":makeQuery(id+"F16.boolean.opBoolean","MERGE",EDGE,{"derivedFrom":[makeQuery(id+"F15.opExtrude","SWEPT_EDGE",EDGE,{"disambiguationData":[OSD([subQ2,subQ0,subQ1])]}),makeQuery(id+"F16.opExtrude","SWEPT_EDGE",EDGE,{"disambiguationData":[OSD([subQ2,subQ0,subQ1])]})]})});}
            var Q30;
            {var subQ0=sQuery(id+"F14.wireOp",EDGE,"E36");var subQ1=sQuery(id+"F14.wireOp",EDGE,"E37");var subQ2=sQuery(id+"F14.wireOp",EDGE,"E24");Q30=makeQuery(id+"F18.boolean.opBoolean","SPLIT",EDGE,{"disambiguationData":[TD([makeQuery(id+"F18.opExtrude","SWEPT_FACE",FACE,{"disambiguationData":[OSD([sQuery(id+"F17.wireOp",EDGE,"E50.right")])]})])],"derivedFrom":makeQuery(id+"F16.boolean.opBoolean","MERGE",EDGE,{"derivedFrom":[makeQuery(id+"F15.opExtrude","SWEPT_EDGE",EDGE,{"disambiguationData":[OSD([subQ2,subQ0,subQ1])]}),makeQuery(id+"F16.opExtrude","SWEPT_EDGE",EDGE,{"disambiguationData":[OSD([subQ2,subQ0,subQ1])]})]})});}
            var Q31;
            Q31=makeQuery(id+"F16.opExtrude","CAP_EDGE",EDGE,{"disambiguationData":[OSD([sQuery(id+"F14.wireOp",EDGE,"E37")])],"isStart":false});
            var Q32;
            {var subQ0=sQuery(id+"F14.wireOp",EDGE,"E38");var subQ1=sQuery(id+"F14.wireOp",EDGE,"E41");var subQ2=sQuery(id+"F14.wireOp",EDGE,"E24");Q32=makeQuery(id+"F18.boolean.opBoolean","SPLIT",EDGE,{"disambiguationData":[TD([makeQuery(id+"F18.opExtrude","SWEPT_FACE",FACE,{"disambiguationData":[OSD([sQuery(id+"F17.wireOp",EDGE,"E50.right")])]})])],"derivedFrom":makeQuery(id+"F16.boolean.opBoolean","MERGE",EDGE,{"derivedFrom":[makeQuery(id+"F15.opExtrude","SWEPT_EDGE",EDGE,{"disambiguationData":[OSD([subQ2,subQ0,subQ1])]}),makeQuery(id+"F16.opExtrude","SWEPT_EDGE",EDGE,{"disambiguationData":[OSD([subQ2,subQ0,subQ1])]})]})});}
            var Q33;
            Q33=makeQuery(id+"F16.opExtrude","CAP_EDGE",EDGE,{"disambiguationData":[OSD([sQuery(id+"F14.wireOp",EDGE,"E41")])],"isStart":false});
            var Q34;
            {var subQ0=sQuery(id+"F14.wireOp",EDGE,"E41");var subQ1=sQuery(id+"F14.wireOp",EDGE,"E40");var subQ2=sQuery(id+"F14.wireOp",EDGE,"E24");Q34=makeQuery(id+"F18.boolean.opBoolean","SPLIT",EDGE,{"disambiguationData":[TD([makeQuery(id+"F18.opExtrude","SWEPT_FACE",FACE,{"disambiguationData":[OSD([sQuery(id+"F17.wireOp",EDGE,"E50.right")])]})])],"derivedFrom":makeQuery(id+"F16.boolean.opBoolean","MERGE",EDGE,{"derivedFrom":[makeQuery(id+"F15.opExtrude","SWEPT_EDGE",EDGE,{"disambiguationData":[OSD([subQ2,subQ1,subQ0])]}),makeQuery(id+"F16.opExtrude","SWEPT_EDGE",EDGE,{"disambiguationData":[OSD([subQ2,subQ1,subQ0])]})]})});}
            var Q35;
            {var subQ0=sQuery(id+"F14.wireOp",EDGE,"E41");var subQ1=sQuery(id+"F14.wireOp",EDGE,"E38");var subQ2=sQuery(id+"F14.wireOp",EDGE,"E24");Q35=makeQuery(id+"F18.boolean.opBoolean","SPLIT",EDGE,{"disambiguationData":[TD([makeQuery(id+"F18.opExtrude","SWEPT_FACE",FACE,{"disambiguationData":[OSD([sQuery(id+"F17.wireOp",EDGE,"E50.left")])]})])],"derivedFrom":makeQuery(id+"F16.boolean.opBoolean","MERGE",EDGE,{"derivedFrom":[makeQuery(id+"F15.opExtrude","SWEPT_EDGE",EDGE,{"disambiguationData":[OSD([subQ2,subQ1,subQ0])]}),makeQuery(id+"F16.opExtrude","SWEPT_EDGE",EDGE,{"disambiguationData":[OSD([subQ2,subQ1,subQ0])]})]})});}
            var Q36;
            {var subQ0=sQuery(id+"F14.wireOp",EDGE,"E41");var subQ1=sQuery(id+"F14.wireOp",EDGE,"E40");var subQ2=sQuery(id+"F14.wireOp",EDGE,"E24");Q36=makeQuery(id+"F18.boolean.opBoolean","SPLIT",EDGE,{"disambiguationData":[TD([makeQuery(id+"F18.opExtrude","SWEPT_FACE",FACE,{"disambiguationData":[OSD([sQuery(id+"F17.wireOp",EDGE,"E50.left")])]})])],"derivedFrom":makeQuery(id+"F16.boolean.opBoolean","MERGE",EDGE,{"derivedFrom":[makeQuery(id+"F15.opExtrude","SWEPT_EDGE",EDGE,{"disambiguationData":[OSD([subQ2,subQ1,subQ0])]}),makeQuery(id+"F16.opExtrude","SWEPT_EDGE",EDGE,{"disambiguationData":[OSD([subQ2,subQ1,subQ0])]})]})});}
            var Q37;
            Q37=makeQuery(id+"F15.opExtrude","CAP_EDGE",EDGE,{"disambiguationData":[OSD([sQuery(id+"F14.wireOp",EDGE,"E41")])],"isStart":false});
            var Q38;
            {var subQ0=sQuery(id+"F14.wireOp",EDGE,"E49");var subQ1=sQuery(id+"F14.wireOp",EDGE,"E46");var subQ2=sQuery(id+"F14.wireOp",EDGE,"E24");Q38=makeQuery(id+"F18.boolean.opBoolean","SPLIT",EDGE,{"disambiguationData":[TD([makeQuery(id+"F18.opExtrude","SWEPT_FACE",FACE,{"disambiguationData":[OSD([sQuery(id+"F17.wireOp",EDGE,"E50.right")])]})])],"derivedFrom":makeQuery(id+"F16.boolean.opBoolean","MERGE",EDGE,{"derivedFrom":[makeQuery(id+"F15.opExtrude","SWEPT_EDGE",EDGE,{"disambiguationData":[OSD([subQ2,subQ1,subQ0])]}),makeQuery(id+"F16.opExtrude","SWEPT_EDGE",EDGE,{"disambiguationData":[OSD([subQ2,subQ1,subQ0])]})]})});}
            var Q39;
            Q39=makeQuery(id+"F16.opExtrude","CAP_EDGE",EDGE,{"disambiguationData":[OSD([sQuery(id+"F14.wireOp",EDGE,"E46")])],"isStart":false});
            var Q40;
            {var subQ0=sQuery(id+"F14.wireOp",EDGE,"E46");var subQ1=sQuery(id+"F14.wireOp",EDGE,"E47");var subQ2=sQuery(id+"F14.wireOp",EDGE,"E24");Q40=makeQuery(id+"F18.boolean.opBoolean","SPLIT",EDGE,{"disambiguationData":[TD([makeQuery(id+"F18.opExtrude","SWEPT_FACE",FACE,{"disambiguationData":[OSD([sQuery(id+"F17.wireOp",EDGE,"E50.right")])]})])],"derivedFrom":makeQuery(id+"F16.boolean.opBoolean","MERGE",EDGE,{"derivedFrom":[makeQuery(id+"F15.opExtrude","SWEPT_EDGE",EDGE,{"disambiguationData":[OSD([subQ2,subQ0,subQ1])]}),makeQuery(id+"F16.opExtrude","SWEPT_EDGE",EDGE,{"disambiguationData":[OSD([subQ2,subQ0,subQ1])]})]})});}
            var Q41;
            {var subQ0=sQuery(id+"F14.wireOp",EDGE,"E47");var subQ1=sQuery(id+"F14.wireOp",EDGE,"E46");var subQ2=sQuery(id+"F14.wireOp",EDGE,"E24");Q41=makeQuery(id+"F18.boolean.opBoolean","SPLIT",EDGE,{"disambiguationData":[TD([makeQuery(id+"F18.opExtrude","SWEPT_FACE",FACE,{"disambiguationData":[OSD([sQuery(id+"F17.wireOp",EDGE,"E50.left")])]})])],"derivedFrom":makeQuery(id+"F16.boolean.opBoolean","MERGE",EDGE,{"derivedFrom":[makeQuery(id+"F15.opExtrude","SWEPT_EDGE",EDGE,{"disambiguationData":[OSD([subQ2,subQ1,subQ0])]}),makeQuery(id+"F16.opExtrude","SWEPT_EDGE",EDGE,{"disambiguationData":[OSD([subQ2,subQ1,subQ0])]})]})});}
            var Q42;
            {var subQ0=sQuery(id+"F14.wireOp",EDGE,"E46");var subQ1=sQuery(id+"F14.wireOp",EDGE,"E49");var subQ2=sQuery(id+"F14.wireOp",EDGE,"E24");Q42=makeQuery(id+"F18.boolean.opBoolean","SPLIT",EDGE,{"disambiguationData":[TD([makeQuery(id+"F18.opExtrude","SWEPT_FACE",FACE,{"disambiguationData":[OSD([sQuery(id+"F17.wireOp",EDGE,"E50.left")])]})])],"derivedFrom":makeQuery(id+"F16.boolean.opBoolean","MERGE",EDGE,{"derivedFrom":[makeQuery(id+"F15.opExtrude","SWEPT_EDGE",EDGE,{"disambiguationData":[OSD([subQ2,subQ0,subQ1])]}),makeQuery(id+"F16.opExtrude","SWEPT_EDGE",EDGE,{"disambiguationData":[OSD([subQ2,subQ0,subQ1])]})]})});}
            var Q43;
            Q43=makeQuery(id+"F15.opExtrude","CAP_EDGE",EDGE,{"disambiguationData":[OSD([sQuery(id+"F14.wireOp",EDGE,"E46")])],"isStart":false});
            fillet(context, id + "F19", {"entities" : qUnion([Q0, Q1, Q2, Q3, Q4, Q5, Q6, Q7, Q8, Q9, Q10, Q11, Q12, Q13, Q14, Q15, Q16, Q17, Q18, Q19, Q20, Q21, Q22, Q23, Q24, Q25, Q26, Q27, Q28, Q29, Q30, Q31, Q32, Q33, Q34, Q35, Q36, Q37, Q38, Q39, Q40, Q41, Q42, Q43]), "radius" : 0.25 * mm, "tangentPropagation" : true, "allowEdgeOverflow" : false});
        }
        {
            var Q0;
            Q0=makeQuery(id+"F18.opExtrude","CAP_EDGE",EDGE,{"disambiguationData":[OSD([sQuery(id+"F17.wireOp",EDGE,"E50.bottom")])],"isStart":true});
            var Q1;
            Q1=makeQuery(id+"F18.opExtrude","CAP_EDGE",EDGE,{"disambiguationData":[OSD([sQuery(id+"F17.wireOp",EDGE,"E50.top")])],"isStart":true});
            chamfer(context, id + "F20", {"entities" : qUnion([Q0, Q1]), "chamferType" : ChamferType.OFFSET_ANGLE, "width" : 8.38 * mm, "oppositeDirection" : true, "angle" : 11 * degree, "tangentPropagation" : true});
        }
        {
            var Q0;
            {var subQ0=sQuery(id+"F14.wireOp",EDGE,"E25.left");Q0=makeQuery(id+"F18.boolean.opBoolean","MERGE",FACE,{"derivedFrom":[makeQuery(id+"F16.boolean.opBoolean","MERGE",FACE,{"derivedFrom":[makeQuery(id+"F15.opExtrude","SWEPT_FACE",FACE,{"disambiguationData":[OSD([subQ0])]}),makeQuery(id+"F16.opExtrude","SWEPT_FACE",FACE,{"disambiguationData":[OSD([subQ0])]})]}),makeQuery(id+"F18.opExtrude","CAP_FACE",FACE,{"disambiguationData":[OSD([sQuery(id+"F17.wireOp",EDGE,"E50.bottom"),sQuery(id+"F17.wireOp",EDGE,"E50.top"),sQuery(id+"F17.wireOp",EDGE,"E50.left"),sQuery(id+"F17.wireOp",EDGE,"E50.right")])],"isStart":true})]});}
            var sketch = newSketch(context, id + "F21", { "sketchPlane" : qUnion([Q0])});
            skLineSegment(sketch, "E51", {"start": v(1.78, 32.26) * mm, "end": v(1.78, 31.24) * mm});
            skLineSegment(sketch, "E52", {"start": v(3.3, 32.26) * mm, "end": v(3.3, 31.24) * mm});
            skLineSegment(sketch, "E53", {"start": v(3.3, 31.24) * mm, "end": v(3.3, 27.43) * mm});
            skLineSegment(sketch, "E54", {"start": v(3.3, 27.43) * mm, "end": v(1.78, 27.43) * mm});
            skLineSegment(sketch, "E55", {"start": v(1.78, 27.43) * mm, "end": v(1.78, 31.24) * mm});
            skLineSegment(sketch, "E56", {"start": v(1.78, 32.26) * mm, "end": v(1.78, 36.07) * mm});
            skLineSegment(sketch, "E57", {"start": v(1.78, 36.07) * mm, "end": v(3.3, 36.07) * mm});
            skLineSegment(sketch, "E58", {"start": v(3.3, 36.07) * mm, "end": v(3.3, 32.26) * mm});
            skSolve(sketch);
        }
        {
            var Q0;
            Q0=makeQuery(id+"F21.imprint","IMPRINT",FACE,{"disambiguationData":[TD([[makeQuery(id+"F21.imprint","IMPRINT",EDGE,{"derivedFrom":sQuery(id+"F21.wireOp",EDGE,"E51")}),1.0]])]});
            extrude(context, id + "F22", {"entities" : qUnion([Q0]), "operationType" : NewBodyOperationType.REMOVE, "oppositeDirection" : true, "depth" : 0.25 * mm});
        }
        {
            var Q0;
            Q0=makeQuery(id+"F20.opChamfer","BLEND_FACE",FACE,{"disambiguationData":[OSD([sQuery(id+"F17.wireOp",EDGE,"E50.top")])]});
            var Q1;
            Q1=makeQuery(id+"F20.opChamfer","BLEND_FACE",FACE,{"disambiguationData":[OSD([sQuery(id+"F17.wireOp",EDGE,"E50.bottom")])]});
            extrude(context, id + "F23", {"entities" : qUnion([Q0, Q1]), "operationType" : NewBodyOperationType.REMOVE, "oppositeDirection" : true, "depth" : 0.25 * mm});
        }
        {
            var Q0;
            Q0=makeQuery(id+"F23.boolean.opBoolean","COPY",FACE,{"derivedFrom":makeQuery(id+"F23.opExtrude","SWEPT_FACE",FACE,{"disambiguationData":[OSD([sQuery(id+"F14.wireOp",EDGE,"E25.left"),sQuery(id+"F17.wireOp",EDGE,"E50.bottom"),sQuery(id+"F17.wireOp",EDGE,"E50.top"),sQuery(id+"F17.wireOp",EDGE,"E50.left"),sQuery(id+"F17.wireOp",EDGE,"E50.right"),sQuery(id+"F21.wireOp",EDGE,"E54")])]})});
            extrude(context, id + "F24", {"entities" : qUnion([Q0]), "operationType" : NewBodyOperationType.REMOVE, "oppositeDirection" : true, "depth" : 0.05 * mm});
        }
        {
            var Q0;
            Q0=makeQuery(id+"F23.boolean.opBoolean","COPY",FACE,{"derivedFrom":makeQuery(id+"F23.opExtrude","SWEPT_FACE",FACE,{"disambiguationData":[OSD([sQuery(id+"F17.wireOp",EDGE,"E50.top")])]})});
            extrude(context, id + "F25", {"entities" : qUnion([Q0]), "operationType" : NewBodyOperationType.REMOVE, "oppositeDirection" : true, "depth" : 0.05 * mm});
        }
        {
            var Q0;
            {var subQ0=sQuery(id+"F17.wireOp",EDGE,"E50.left");var subQ2=sQuery(id+"F14.wireOp",EDGE,"E46");var subQ4=makeQuery(id+"F15.opExtrude","SWEPT_FACE",FACE,{"disambiguationData":[OSD([subQ2])]});var subQ9=sQuery(id+"F17.wireOp",EDGE,"E50.bottom");Q0=makeQuery(id+"F23.boolean.opBoolean","COPY",FACE,{"disambiguationData":[TD([subQ4])],"derivedFrom":makeQuery(id+"F23.opExtrude","SWEPT_FACE",FACE,{"disambiguationData":[OSD([subQ9,subQ0])]})});}
            var Q1;
            {var subQ0=sQuery(id+"F14.wireOp",EDGE,"E41");var subQ5=makeQuery(id+"F15.opExtrude","SWEPT_FACE",FACE,{"disambiguationData":[OSD([subQ0])]});var subQ6=sQuery(id+"F17.wireOp",EDGE,"E50.left");var subQ9=sQuery(id+"F17.wireOp",EDGE,"E50.bottom");Q1=makeQuery(id+"F23.boolean.opBoolean","COPY",FACE,{"disambiguationData":[TD([subQ5])],"derivedFrom":makeQuery(id+"F23.opExtrude","SWEPT_FACE",FACE,{"disambiguationData":[OSD([subQ9,subQ6])]})});}
            var Q2;
            {var subQ0=sQuery(id+"F14.wireOp",EDGE,"E37");var subQ5=makeQuery(id+"F15.opExtrude","SWEPT_FACE",FACE,{"disambiguationData":[OSD([subQ0])]});var subQ8=sQuery(id+"F21.wireOp",EDGE,"E58");var subQ9=sQuery(id+"F21.wireOp",EDGE,"E53");var subQ10=sQuery(id+"F21.wireOp",EDGE,"E52");Q2=makeQuery(id+"F22.boolean.opBoolean","COPY",FACE,{"disambiguationData":[TD([subQ5])],"derivedFrom":makeQuery(id+"F22.opExtrude","SWEPT_FACE",FACE,{"disambiguationData":[OSD([subQ10,subQ9,subQ8])]})});}
            var Q3;
            {var subQ8=sQuery(id+"F14.wireOp",EDGE,"E25.bottom");var subQ13=makeQuery(id+"F15.opExtrude","SWEPT_FACE",FACE,{"disambiguationData":[OSD([subQ8])]});var subQ14=sQuery(id+"F21.wireOp",EDGE,"E58");var subQ15=sQuery(id+"F21.wireOp",EDGE,"E53");var subQ16=sQuery(id+"F21.wireOp",EDGE,"E52");Q3=makeQuery(id+"F22.boolean.opBoolean","COPY",FACE,{"disambiguationData":[TD([subQ13])],"derivedFrom":makeQuery(id+"F22.opExtrude","SWEPT_FACE",FACE,{"disambiguationData":[OSD([subQ16,subQ15,subQ14])]})});}
            var Q4;
            {var subQ0=sQuery(id+"F14.wireOp",EDGE,"E28");var subQ2=makeQuery(id+"F15.opExtrude","SWEPT_FACE",FACE,{"disambiguationData":[OSD([subQ0])]});var subQ8=sQuery(id+"F21.wireOp",EDGE,"E58");var subQ9=sQuery(id+"F21.wireOp",EDGE,"E53");var subQ10=sQuery(id+"F21.wireOp",EDGE,"E52");Q4=makeQuery(id+"F22.boolean.opBoolean","COPY",FACE,{"disambiguationData":[TD([subQ2])],"derivedFrom":makeQuery(id+"F22.opExtrude","SWEPT_FACE",FACE,{"disambiguationData":[OSD([subQ10,subQ9,subQ8])]})});}
            var Q5;
            {var subQ1=sQuery(id+"F14.wireOp",EDGE,"E30");var subQ3=makeQuery(id+"F15.opExtrude","SWEPT_FACE",FACE,{"disambiguationData":[OSD([subQ1])]});var subQ7=sQuery(id+"F17.wireOp",EDGE,"E50.left");var subQ9=sQuery(id+"F17.wireOp",EDGE,"E50.top");Q5=makeQuery(id+"F23.boolean.opBoolean","COPY",FACE,{"disambiguationData":[TD([subQ3])],"derivedFrom":makeQuery(id+"F23.opExtrude","SWEPT_FACE",FACE,{"disambiguationData":[OSD([subQ9,subQ7])]})});}
            var Q6;
            {var subQ0=sQuery(id+"F14.wireOp",EDGE,"E42");var subQ5=makeQuery(id+"F15.opExtrude","SWEPT_FACE",FACE,{"disambiguationData":[OSD([subQ0])]});var subQ6=sQuery(id+"F17.wireOp",EDGE,"E50.left");var subQ9=sQuery(id+"F17.wireOp",EDGE,"E50.top");Q6=makeQuery(id+"F23.boolean.opBoolean","COPY",FACE,{"disambiguationData":[TD([subQ5])],"derivedFrom":makeQuery(id+"F23.opExtrude","SWEPT_FACE",FACE,{"disambiguationData":[OSD([subQ9,subQ6])]})});}
            extrude(context, id + "F26", {"entities" : qUnion([Q0, Q1, Q2, Q3, Q4, Q5, Q6]), "operationType" : NewBodyOperationType.ADD, "depth" : 5.08 * mm});
        }
        {
            var Q0;
            {var subQ0=sQuery(id+"F17.wireOp",EDGE,"E50.left");var subQ1=sQuery(id+"F17.wireOp",EDGE,"E50.bottom");var subQ2=makeQuery(id+"F18.opExtrude","SWEPT_FACE",FACE,{"disambiguationData":[OSD([subQ0])]});var subQ6=makeQuery(id+"F23.opExtrude","CAP_FACE",FACE,{"disambiguationData":[OSD([subQ1]),OD(1.0)],"isStart":false});Q0=makeQuery(id+"F23.boolean.opBoolean","COPY",EDGE,{"disambiguationData":[topologyDisambiguationEdgeConnected([subQ2,subQ6]),TD([makeQuery(id+"F18.opExtrude","SWEPT_FACE",FACE,{"disambiguationData":[OSD([subQ1])]})])],"derivedFrom":makeQuery(id+"F23.opExtrude","CAP_EDGE",EDGE,{"disambiguationData":[OSD([subQ1,subQ0]),OD(1.0)],"isStart":false})});}
            var Q1;
            {var subQ0=sQuery(id+"F17.wireOp",EDGE,"E50.bottom");Q1=makeQuery(id+"F23.boolean.opBoolean","INTERSECT",EDGE,{"derivedFrom":[makeQuery(id+"F18.opExtrude","SWEPT_FACE",FACE,{"disambiguationData":[OSD([subQ0])]}),makeQuery(id+"F23.opExtrude","CAP_FACE",FACE,{"disambiguationData":[OSD([subQ0]),OD(1.0)],"isStart":false})]});}
            var Q2;
            {var subQ2=sQuery(id+"F17.wireOp",EDGE,"E50.right");var subQ3=makeQuery(id+"F18.opExtrude","SWEPT_FACE",FACE,{"disambiguationData":[OSD([subQ2])]});var subQ5=sQuery(id+"F17.wireOp",EDGE,"E50.bottom");var subQ6=makeQuery(id+"F23.opExtrude","CAP_FACE",FACE,{"disambiguationData":[OSD([subQ5]),OD(1.0)],"isStart":false});Q2=makeQuery(id+"F23.boolean.opBoolean","COPY",EDGE,{"disambiguationData":[topologyDisambiguationEdgeConnected([subQ3,subQ6]),TD([makeQuery(id+"F18.opExtrude","SWEPT_FACE",FACE,{"disambiguationData":[OSD([subQ5])]})])],"derivedFrom":makeQuery(id+"F23.opExtrude","CAP_EDGE",EDGE,{"disambiguationData":[OSD([subQ5,subQ2]),OD(1.0)],"isStart":false})});}
            var Q3;
            {var subQ1=sQuery(id+"F17.wireOp",EDGE,"E50.right");var subQ2=makeQuery(id+"F18.opExtrude","SWEPT_FACE",FACE,{"disambiguationData":[OSD([subQ1])]});var subQ4=sQuery(id+"F14.wireOp",EDGE,"E24");var subQ5=sQuery(id+"F17.wireOp",EDGE,"E50.bottom");var subQ6=sQuery(id+"F14.wireOp",EDGE,"E41");var subQ7=sQuery(id+"F14.wireOp",EDGE,"E40");var subQ8=makeQuery(id+"F23.opExtrude","CAP_FACE",FACE,{"disambiguationData":[OSD([subQ5]),OD(1.0)],"isStart":false});Q3=makeQuery(id+"F23.boolean.opBoolean","COPY",EDGE,{"disambiguationData":[topologyDisambiguationEdgeConnected([subQ2,subQ8]),TD([makeQuery(id+"F19.opFillet","BLEND_FACE",FACE,{"disambiguationData":[OSD([subQ4,subQ7,subQ6]),TDD([makeQuery(id+"F18.boolean.opBoolean","SPLIT",EDGE,{"disambiguationData":[TD([subQ2])],"derivedFrom":makeQuery(id+"F16.boolean.opBoolean","MERGE",EDGE,{"derivedFrom":[makeQuery(id+"F15.opExtrude","SWEPT_EDGE",EDGE,{"disambiguationData":[OSD([subQ4,subQ7,subQ6])]}),makeQuery(id+"F16.opExtrude","SWEPT_EDGE",EDGE,{"disambiguationData":[OSD([subQ4,subQ7,subQ6])]})]})})])]})])],"derivedFrom":makeQuery(id+"F23.opExtrude","CAP_EDGE",EDGE,{"disambiguationData":[OSD([subQ5,subQ1]),OD(1.0)],"isStart":false})});}
            var Q4;
            {var subQ2=sQuery(id+"F17.wireOp",EDGE,"E50.left");var subQ3=makeQuery(id+"F18.opExtrude","SWEPT_FACE",FACE,{"disambiguationData":[OSD([subQ2])]});var subQ4=sQuery(id+"F14.wireOp",EDGE,"E24");var subQ5=sQuery(id+"F17.wireOp",EDGE,"E50.bottom");var subQ6=sQuery(id+"F14.wireOp",EDGE,"E41");var subQ7=sQuery(id+"F14.wireOp",EDGE,"E40");var subQ8=makeQuery(id+"F23.opExtrude","CAP_FACE",FACE,{"disambiguationData":[OSD([subQ5]),OD(1.0)],"isStart":false});Q4=makeQuery(id+"F23.boolean.opBoolean","COPY",EDGE,{"disambiguationData":[topologyDisambiguationEdgeConnected([subQ3,subQ8]),TD([makeQuery(id+"F19.opFillet","BLEND_FACE",FACE,{"disambiguationData":[OSD([subQ4,subQ7,subQ6]),TDD([makeQuery(id+"F18.boolean.opBoolean","SPLIT",EDGE,{"disambiguationData":[TD([subQ3])],"derivedFrom":makeQuery(id+"F16.boolean.opBoolean","MERGE",EDGE,{"derivedFrom":[makeQuery(id+"F15.opExtrude","SWEPT_EDGE",EDGE,{"disambiguationData":[OSD([subQ4,subQ7,subQ6])]}),makeQuery(id+"F16.opExtrude","SWEPT_EDGE",EDGE,{"disambiguationData":[OSD([subQ4,subQ7,subQ6])]})]})})])]})])],"derivedFrom":makeQuery(id+"F23.opExtrude","CAP_EDGE",EDGE,{"disambiguationData":[OSD([subQ5,subQ2]),OD(1.0)],"isStart":false})});}
            var Q5;
            {var subQ0=sQuery(id+"F17.wireOp",EDGE,"E50.right");var subQ1=sQuery(id+"F17.wireOp",EDGE,"E50.bottom");var subQ4=makeQuery(id+"F18.opExtrude","SWEPT_FACE",FACE,{"disambiguationData":[OSD([subQ0])]});var subQ6=makeQuery(id+"F23.opExtrude","CAP_FACE",FACE,{"disambiguationData":[OSD([subQ1]),OD(1.0)],"isStart":false});Q5=makeQuery(id+"F23.boolean.opBoolean","COPY",EDGE,{"disambiguationData":[topologyDisambiguationEdgeConnected([subQ4,subQ6]),TD([makeQuery(id+"F23.opExtrude","SWEPT_FACE",FACE,{"disambiguationData":[OSD([sQuery(id+"F14.wireOp",EDGE,"E25.left"),subQ1,sQuery(id+"F17.wireOp",EDGE,"E50.top"),sQuery(id+"F17.wireOp",EDGE,"E50.left"),subQ0,sQuery(id+"F21.wireOp",EDGE,"E54")])]})])],"derivedFrom":makeQuery(id+"F23.opExtrude","CAP_EDGE",EDGE,{"disambiguationData":[OSD([subQ1,subQ0]),OD(1.0)],"isStart":false})});}
            var Q6;
            {var subQ0=sQuery(id+"F17.wireOp",EDGE,"E50.left");var subQ1=sQuery(id+"F17.wireOp",EDGE,"E50.bottom");var subQ4=makeQuery(id+"F18.opExtrude","SWEPT_FACE",FACE,{"disambiguationData":[OSD([subQ0])]});var subQ6=makeQuery(id+"F23.opExtrude","CAP_FACE",FACE,{"disambiguationData":[OSD([subQ1]),OD(1.0)],"isStart":false});Q6=makeQuery(id+"F23.boolean.opBoolean","COPY",EDGE,{"disambiguationData":[topologyDisambiguationEdgeConnected([subQ4,subQ6]),TD([makeQuery(id+"F23.opExtrude","SWEPT_FACE",FACE,{"disambiguationData":[OSD([sQuery(id+"F14.wireOp",EDGE,"E25.left"),subQ1,sQuery(id+"F17.wireOp",EDGE,"E50.top"),subQ0,sQuery(id+"F17.wireOp",EDGE,"E50.right"),sQuery(id+"F21.wireOp",EDGE,"E54")])]})])],"derivedFrom":makeQuery(id+"F23.opExtrude","CAP_EDGE",EDGE,{"disambiguationData":[OSD([subQ1,subQ0]),OD(1.0)],"isStart":false})});}
            var Q7;
            {var subQ1=sQuery(id+"F14.wireOp",EDGE,"E25.top");var subQ2=sQuery(id+"F17.wireOp",EDGE,"E50.right");var subQ3=makeQuery(id+"F18.opExtrude","SWEPT_FACE",FACE,{"disambiguationData":[OSD([subQ2])]});var subQ5=makeQuery(id+"F15.opExtrude","SWEPT_FACE",FACE,{"disambiguationData":[OSD([subQ1])]});var subQ7=sQuery(id+"F21.wireOp",EDGE,"E56");var subQ8=sQuery(id+"F21.wireOp",EDGE,"E55");var subQ9=sQuery(id+"F21.wireOp",EDGE,"E51");var subQ10=makeQuery(id+"F22.opExtrude","CAP_FACE",FACE,{"disambiguationData":[OSD([subQ9,sQuery(id+"F21.wireOp",EDGE,"E52"),sQuery(id+"F21.wireOp",EDGE,"E53"),sQuery(id+"F21.wireOp",EDGE,"E54"),subQ8,subQ7,sQuery(id+"F21.wireOp",EDGE,"E57"),sQuery(id+"F21.wireOp",EDGE,"E58")])],"isStart":false});Q7=makeQuery(id+"F22.boolean.opBoolean","COPY",EDGE,{"disambiguationData":[topologyDisambiguationEdgeConnected([subQ3,subQ10]),TD([subQ5])],"derivedFrom":makeQuery(id+"F22.opExtrude","CAP_EDGE",EDGE,{"disambiguationData":[OSD([subQ9,subQ8,subQ7])],"isStart":false})});}
            var Q8;
            {var subQ1=sQuery(id+"F14.wireOp",EDGE,"E25.top");var subQ2=makeQuery(id+"F15.opExtrude","SWEPT_FACE",FACE,{"disambiguationData":[OSD([subQ1])]});var subQ4=sQuery(id+"F17.wireOp",EDGE,"E50.left");var subQ5=makeQuery(id+"F18.opExtrude","SWEPT_FACE",FACE,{"disambiguationData":[OSD([subQ4])]});var subQ9=sQuery(id+"F21.wireOp",EDGE,"E58");var subQ10=sQuery(id+"F21.wireOp",EDGE,"E53");var subQ11=sQuery(id+"F21.wireOp",EDGE,"E52");var subQ12=makeQuery(id+"F22.opExtrude","CAP_FACE",FACE,{"disambiguationData":[OSD([sQuery(id+"F21.wireOp",EDGE,"E51"),subQ11,subQ10,sQuery(id+"F21.wireOp",EDGE,"E54"),sQuery(id+"F21.wireOp",EDGE,"E55"),sQuery(id+"F21.wireOp",EDGE,"E56"),sQuery(id+"F21.wireOp",EDGE,"E57"),subQ9])],"isStart":false});Q8=makeQuery(id+"F22.boolean.opBoolean","COPY",EDGE,{"disambiguationData":[topologyDisambiguationEdgeConnected([subQ5,subQ12]),TD([subQ2])],"derivedFrom":makeQuery(id+"F22.opExtrude","CAP_EDGE",EDGE,{"disambiguationData":[OSD([subQ11,subQ10,subQ9])],"isStart":false})});}
            var Q9;
            {var subQ1=sQuery(id+"F14.wireOp",EDGE,"E25.bottom");var subQ3=makeQuery(id+"F15.opExtrude","SWEPT_FACE",FACE,{"disambiguationData":[OSD([subQ1])]});var subQ4=sQuery(id+"F17.wireOp",EDGE,"E50.left");var subQ5=makeQuery(id+"F18.opExtrude","SWEPT_FACE",FACE,{"disambiguationData":[OSD([subQ4])]});var subQ7=sQuery(id+"F21.wireOp",EDGE,"E58");var subQ8=sQuery(id+"F21.wireOp",EDGE,"E53");var subQ9=sQuery(id+"F21.wireOp",EDGE,"E52");var subQ10=makeQuery(id+"F22.opExtrude","CAP_FACE",FACE,{"disambiguationData":[OSD([sQuery(id+"F21.wireOp",EDGE,"E51"),subQ9,subQ8,sQuery(id+"F21.wireOp",EDGE,"E54"),sQuery(id+"F21.wireOp",EDGE,"E55"),sQuery(id+"F21.wireOp",EDGE,"E56"),sQuery(id+"F21.wireOp",EDGE,"E57"),subQ7])],"isStart":false});Q9=makeQuery(id+"F22.boolean.opBoolean","COPY",EDGE,{"disambiguationData":[topologyDisambiguationEdgeConnected([subQ5,subQ10]),TD([subQ3])],"derivedFrom":makeQuery(id+"F22.opExtrude","CAP_EDGE",EDGE,{"disambiguationData":[OSD([subQ9,subQ8,subQ7])],"isStart":false})});}
            var Q10;
            {var subQ0=sQuery(id+"F17.wireOp",EDGE,"E50.right");var subQ1=makeQuery(id+"F18.opExtrude","SWEPT_FACE",FACE,{"disambiguationData":[OSD([subQ0])]});var subQ2=sQuery(id+"F14.wireOp",EDGE,"E25.bottom");var subQ4=sQuery(id+"F21.wireOp",EDGE,"E56");var subQ5=sQuery(id+"F21.wireOp",EDGE,"E55");var subQ6=sQuery(id+"F21.wireOp",EDGE,"E51");var subQ7=makeQuery(id+"F22.opExtrude","CAP_FACE",FACE,{"disambiguationData":[OSD([subQ6,sQuery(id+"F21.wireOp",EDGE,"E52"),sQuery(id+"F21.wireOp",EDGE,"E53"),sQuery(id+"F21.wireOp",EDGE,"E54"),subQ5,subQ4,sQuery(id+"F21.wireOp",EDGE,"E57"),sQuery(id+"F21.wireOp",EDGE,"E58")])],"isStart":false});var subQ9=makeQuery(id+"F15.opExtrude","SWEPT_FACE",FACE,{"disambiguationData":[OSD([subQ2])]});Q10=makeQuery(id+"F22.boolean.opBoolean","COPY",EDGE,{"disambiguationData":[topologyDisambiguationEdgeConnected([subQ1,subQ7]),TD([subQ9])],"derivedFrom":makeQuery(id+"F22.opExtrude","CAP_EDGE",EDGE,{"disambiguationData":[OSD([subQ6,subQ5,subQ4])],"isStart":false})});}
            var Q11;
            {var subQ0=sQuery(id+"F17.wireOp",EDGE,"E50.right");var subQ1=sQuery(id+"F17.wireOp",EDGE,"E50.top");var subQ2=makeQuery(id+"F23.opExtrude","CAP_FACE",FACE,{"disambiguationData":[OSD([subQ1])],"isStart":false});var subQ3=sQuery(id+"F14.wireOp",EDGE,"E33");var subQ4=makeQuery(id+"F18.opExtrude","SWEPT_FACE",FACE,{"disambiguationData":[OSD([subQ0])]});var subQ5=sQuery(id+"F14.wireOp",EDGE,"E30");var subQ6=sQuery(id+"F14.wireOp",EDGE,"E24");Q11=makeQuery(id+"F23.boolean.opBoolean","COPY",EDGE,{"disambiguationData":[topologyDisambiguationEdgeConnected([subQ4,subQ2]),TD([makeQuery(id+"F19.opFillet","BLEND_FACE",FACE,{"disambiguationData":[OSD([subQ6,subQ5,subQ3]),TDD([makeQuery(id+"F18.boolean.opBoolean","SPLIT",EDGE,{"disambiguationData":[TD([subQ4])],"derivedFrom":makeQuery(id+"F16.boolean.opBoolean","MERGE",EDGE,{"derivedFrom":[makeQuery(id+"F15.opExtrude","SWEPT_EDGE",EDGE,{"disambiguationData":[OSD([subQ6,subQ5,subQ3])]}),makeQuery(id+"F16.opExtrude","SWEPT_EDGE",EDGE,{"disambiguationData":[OSD([subQ6,subQ5,subQ3])]})]})})])]})])],"derivedFrom":makeQuery(id+"F23.opExtrude","CAP_EDGE",EDGE,{"disambiguationData":[OSD([subQ1,subQ0])],"isStart":false})});}
            var Q12;
            {var subQ0=sQuery(id+"F17.wireOp",EDGE,"E50.left");var subQ1=sQuery(id+"F17.wireOp",EDGE,"E50.top");var subQ2=makeQuery(id+"F23.opExtrude","CAP_FACE",FACE,{"disambiguationData":[OSD([subQ1])],"isStart":false});var subQ3=sQuery(id+"F14.wireOp",EDGE,"E33");var subQ4=sQuery(id+"F14.wireOp",EDGE,"E30");var subQ5=sQuery(id+"F14.wireOp",EDGE,"E24");var subQ6=makeQuery(id+"F18.opExtrude","SWEPT_FACE",FACE,{"disambiguationData":[OSD([subQ0])]});Q12=makeQuery(id+"F23.boolean.opBoolean","COPY",EDGE,{"disambiguationData":[topologyDisambiguationEdgeConnected([subQ6,subQ2]),TD([makeQuery(id+"F19.opFillet","BLEND_FACE",FACE,{"disambiguationData":[OSD([subQ5,subQ4,subQ3]),TDD([makeQuery(id+"F18.boolean.opBoolean","SPLIT",EDGE,{"disambiguationData":[TD([subQ6])],"derivedFrom":makeQuery(id+"F16.boolean.opBoolean","MERGE",EDGE,{"derivedFrom":[makeQuery(id+"F15.opExtrude","SWEPT_EDGE",EDGE,{"disambiguationData":[OSD([subQ5,subQ4,subQ3])]}),makeQuery(id+"F16.opExtrude","SWEPT_EDGE",EDGE,{"disambiguationData":[OSD([subQ5,subQ4,subQ3])]})]})})])]})])],"derivedFrom":makeQuery(id+"F23.opExtrude","CAP_EDGE",EDGE,{"disambiguationData":[OSD([subQ1,subQ0])],"isStart":false})});}
            var Q13;
            {var subQ0=sQuery(id+"F17.wireOp",EDGE,"E50.left");var subQ1=sQuery(id+"F17.wireOp",EDGE,"E50.top");var subQ2=sQuery(id+"F14.wireOp",EDGE,"E31");var subQ3=sQuery(id+"F14.wireOp",EDGE,"E24");var subQ4=makeQuery(id+"F18.opExtrude","SWEPT_FACE",FACE,{"disambiguationData":[OSD([subQ0])]});var subQ7=makeQuery(id+"F23.opExtrude","CAP_FACE",FACE,{"disambiguationData":[OSD([subQ1])],"isStart":false});Q13=makeQuery(id+"F23.boolean.opBoolean","COPY",EDGE,{"disambiguationData":[topologyDisambiguationEdgeConnected([subQ4,subQ7]),TD([makeQuery(id+"F19.opFillet","BLEND_FACE",FACE,{"disambiguationData":[OSD([subQ3,subQ2]),TDD([makeQuery(id+"F18.boolean.opBoolean","SPLIT",EDGE,{"disambiguationData":[TD([subQ4])],"derivedFrom":makeQuery(id+"F16.boolean.opBoolean","MERGE",EDGE,{"derivedFrom":[makeQuery(id+"F15.opExtrude","SWEPT_EDGE",EDGE,{"disambiguationData":[OSD([subQ3,subQ2])]}),makeQuery(id+"F16.opExtrude","SWEPT_EDGE",EDGE,{"disambiguationData":[OSD([subQ3,subQ2])]})]})})])]})])],"derivedFrom":makeQuery(id+"F23.opExtrude","CAP_EDGE",EDGE,{"disambiguationData":[OSD([subQ1,subQ0])],"isStart":false})});}
            var Q14;
            {var subQ0=sQuery(id+"F17.wireOp",EDGE,"E50.right");var subQ1=sQuery(id+"F17.wireOp",EDGE,"E50.top");var subQ2=sQuery(id+"F14.wireOp",EDGE,"E31");var subQ3=sQuery(id+"F14.wireOp",EDGE,"E24");var subQ4=makeQuery(id+"F18.opExtrude","SWEPT_FACE",FACE,{"disambiguationData":[OSD([subQ0])]});var subQ7=makeQuery(id+"F23.opExtrude","CAP_FACE",FACE,{"disambiguationData":[OSD([subQ1])],"isStart":false});Q14=makeQuery(id+"F23.boolean.opBoolean","COPY",EDGE,{"disambiguationData":[topologyDisambiguationEdgeConnected([subQ4,subQ7]),TD([makeQuery(id+"F19.opFillet","BLEND_FACE",FACE,{"disambiguationData":[OSD([subQ3,subQ2]),TDD([makeQuery(id+"F18.boolean.opBoolean","SPLIT",EDGE,{"disambiguationData":[TD([subQ4])],"derivedFrom":makeQuery(id+"F16.boolean.opBoolean","MERGE",EDGE,{"derivedFrom":[makeQuery(id+"F15.opExtrude","SWEPT_EDGE",EDGE,{"disambiguationData":[OSD([subQ3,subQ2])]}),makeQuery(id+"F16.opExtrude","SWEPT_EDGE",EDGE,{"disambiguationData":[OSD([subQ3,subQ2])]})]})})])]})])],"derivedFrom":makeQuery(id+"F23.opExtrude","CAP_EDGE",EDGE,{"disambiguationData":[OSD([subQ1,subQ0])],"isStart":false})});}
            var Q15;
            {var subQ0=sQuery(id+"F17.wireOp",EDGE,"E50.right");var subQ1=sQuery(id+"F17.wireOp",EDGE,"E50.top");var subQ4=makeQuery(id+"F18.opExtrude","SWEPT_FACE",FACE,{"disambiguationData":[OSD([subQ0])]});var subQ6=makeQuery(id+"F23.opExtrude","CAP_FACE",FACE,{"disambiguationData":[OSD([subQ1])],"isStart":false});Q15=makeQuery(id+"F25.boolean.opBoolean","MERGE",EDGE,{"derivedFrom":[makeQuery(id+"F23.boolean.opBoolean","COPY",EDGE,{"disambiguationData":[topologyDisambiguationEdgeConnected([subQ4,subQ6]),TD([makeQuery(id+"F23.opExtrude","SWEPT_FACE",FACE,{"disambiguationData":[OSD([subQ1])]})])],"derivedFrom":makeQuery(id+"F23.opExtrude","CAP_EDGE",EDGE,{"disambiguationData":[OSD([subQ1,subQ0])],"isStart":false})}),makeQuery(id+"F25.opExtrude","SWEPT_EDGE",EDGE,{"disambiguationData":[OSD([subQ1,subQ0]),TDD([makeQuery(id+"F23.boolean.opBoolean","COPY",VERTEX,{"derivedFrom":makeQuery(id+"F23.opExtrude","CAP_VERTEX",VERTEX,{"disambiguationData":[OSD([subQ1,subQ0])],"isStart":false})})])]})]});}
            var Q16;
            {var subQ0=sQuery(id+"F17.wireOp",EDGE,"E50.top");Q16=makeQuery(id+"F25.boolean.opBoolean","INTERSECT",EDGE,{"derivedFrom":[makeQuery(id+"F18.opExtrude","SWEPT_FACE",FACE,{"disambiguationData":[OSD([subQ0])]}),makeQuery(id+"F25.opExtrude","SWEPT_FACE",FACE,{"disambiguationData":[OSD([subQ0]),TDD([makeQuery(id+"F23.boolean.opBoolean","COPY",EDGE,{"derivedFrom":makeQuery(id+"F23.opExtrude","CAP_EDGE",EDGE,{"disambiguationData":[OSD([subQ0])],"isStart":false})})])]})]});}
            var Q17;
            {var subQ0=sQuery(id+"F17.wireOp",EDGE,"E50.left");var subQ1=sQuery(id+"F17.wireOp",EDGE,"E50.top");var subQ4=makeQuery(id+"F18.opExtrude","SWEPT_FACE",FACE,{"disambiguationData":[OSD([subQ0])]});var subQ6=makeQuery(id+"F23.opExtrude","CAP_FACE",FACE,{"disambiguationData":[OSD([subQ1])],"isStart":false});Q17=makeQuery(id+"F25.boolean.opBoolean","MERGE",EDGE,{"derivedFrom":[makeQuery(id+"F23.boolean.opBoolean","COPY",EDGE,{"disambiguationData":[topologyDisambiguationEdgeConnected([subQ4,subQ6]),TD([makeQuery(id+"F23.opExtrude","SWEPT_FACE",FACE,{"disambiguationData":[OSD([subQ1])]})])],"derivedFrom":makeQuery(id+"F23.opExtrude","CAP_EDGE",EDGE,{"disambiguationData":[OSD([subQ1,subQ0])],"isStart":false})}),makeQuery(id+"F25.opExtrude","SWEPT_EDGE",EDGE,{"disambiguationData":[OSD([subQ1,subQ0]),TDD([makeQuery(id+"F23.boolean.opBoolean","COPY",VERTEX,{"derivedFrom":makeQuery(id+"F23.opExtrude","CAP_VERTEX",VERTEX,{"disambiguationData":[OSD([subQ1,subQ0])],"isStart":false})})])]})]});}
            fillet(context, id + "F27", {"entities" : qUnion([Q0, Q1, Q2, Q3, Q4, Q5, Q6, Q7, Q8, Q9, Q10, Q11, Q12, Q13, Q14, Q15, Q16, Q17]), "radius" : 0.25 * mm, "tangentPropagation" : true, "allowEdgeOverflow" : false});
        }
    });
